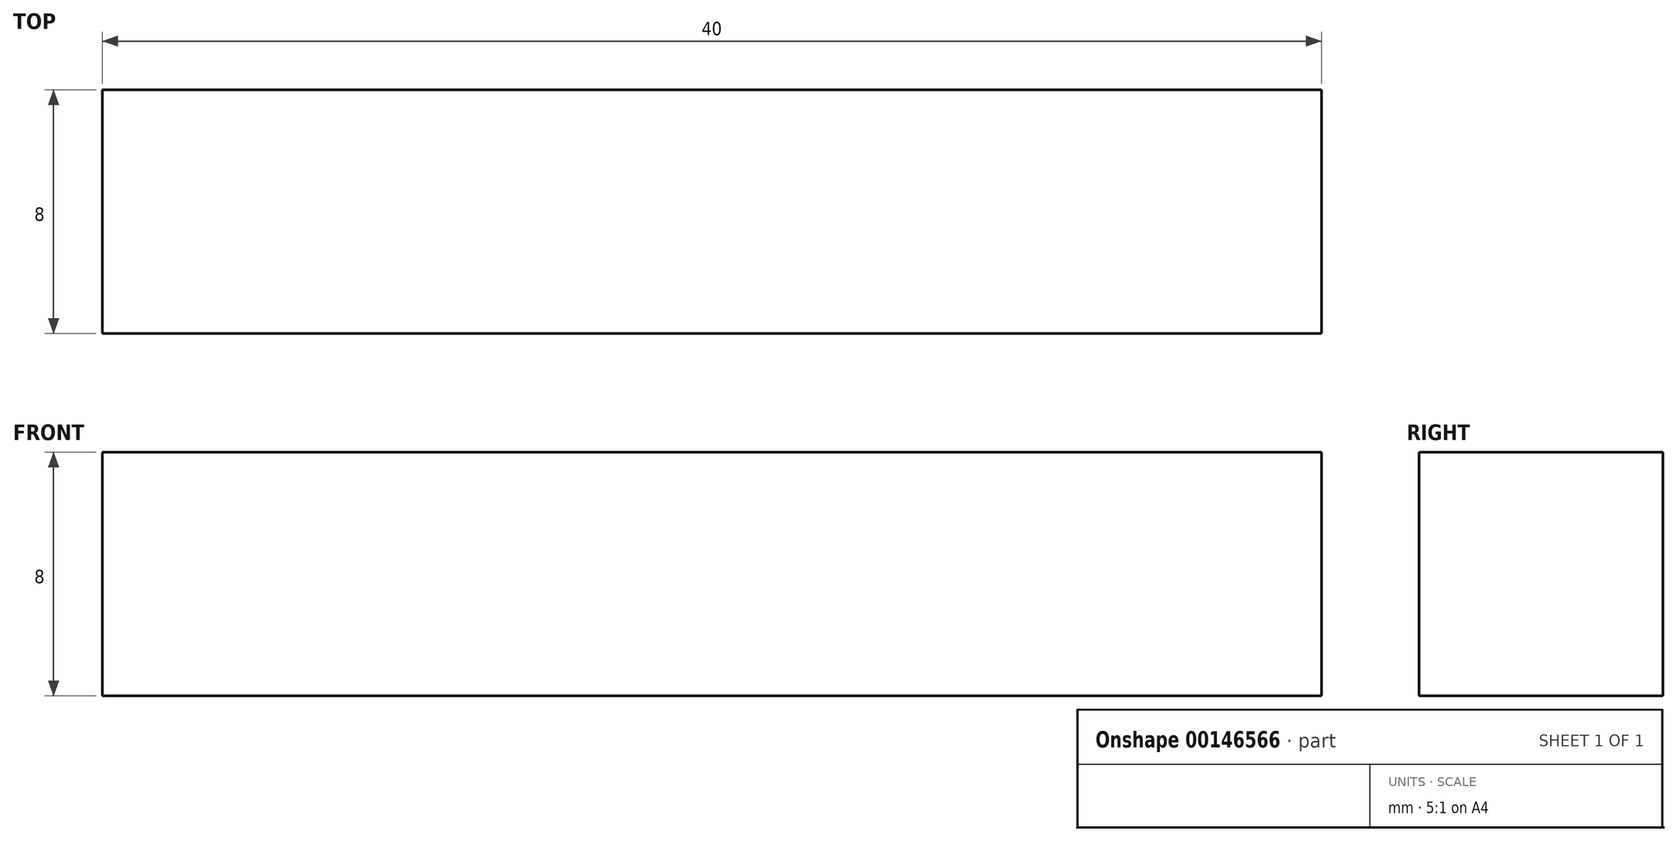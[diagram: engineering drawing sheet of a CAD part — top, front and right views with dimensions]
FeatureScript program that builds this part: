
annotation { "Feature Type Name" : "Feature", "Feature Type Description" : "" }
export const myFeature = defineFeature(function(context is Context, id is Id, definition is map)
    precondition{}
    {
        {
            assignVariable(context, id + "F0", {"name" : "width", "anyValue" : 8});
        }
        {
            var Q0;
            Q0=qCreatedBy(makeId("Front.planeOp"),FACE);
            var sketch = newSketch(context, id + "F1", { "sketchPlane" : qUnion([Q0])});
            skLineSegment(sketch, "E0", {"start": v(-20, 0) * mm, "end": v(-20, 8) * mm});
            skLineSegment(sketch, "E1", {"start": v(-20, 8) * mm, "end": v(20, 8) * mm});
            skLineSegment(sketch, "E2", {"start": v(20, 8) * mm, "end": v(20, 0) * mm});
            skLineSegment(sketch, "E3", {"start": v(20, 0) * mm, "end": v(-20, 0) * mm});
            skSolve(sketch);
        }
        {
            var Q0;
            Q0=makeQuery(id+"F1.imprint","IMPRINT",FACE,{"disambiguationData":[TD([[makeQuery(id+"F1.imprint","IMPRINT",EDGE,{"derivedFrom":sQuery(id+"F1.wireOp",EDGE,"E0")}),-1.0]])]});
            extrude(context, id + "F2", {"entities" : qUnion([Q0]), "depth" : (getVariable(context, 'width')) * mm, "symmetric" : true});
        }
    });
